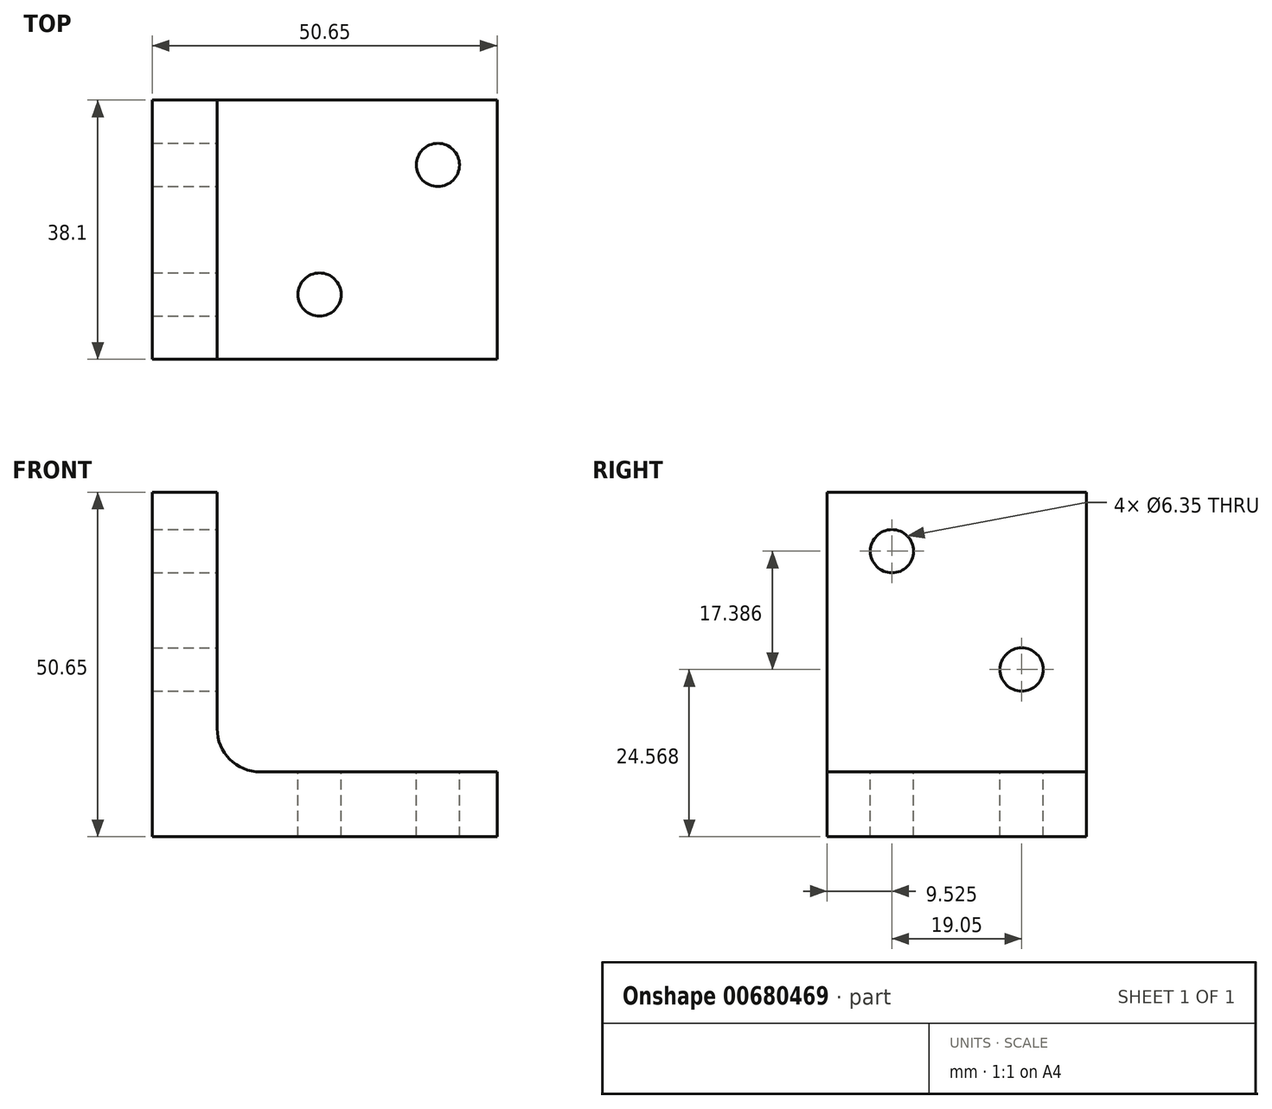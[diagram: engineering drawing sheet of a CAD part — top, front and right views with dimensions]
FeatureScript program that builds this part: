
annotation { "Feature Type Name" : "Feature", "Feature Type Description" : "" }
export const myFeature = defineFeature(function(context is Context, id is Id, definition is map)
    precondition{}
    {
        {
            var Q0;
            Q0=qCreatedBy(makeId("Front.planeOp"),FACE);
            var sketch = newSketch(context, id + "F0", { "sketchPlane" : qUnion([Q0])});
            skLineSegment(sketch, "E0.bottom", {"start": v(0, 0) * mm, "end": v(50.65, 0) * mm});
            skLineSegment(sketch, "E0.top", {"start": v(0, 50.65) * mm, "end": v(50.65, 50.65) * mm});
            skLineSegment(sketch, "E0.left", {"start": v(0, 0) * mm, "end": v(0, 50.65) * mm});
            skLineSegment(sketch, "E0.right", {"start": v(50.65, 0) * mm, "end": v(50.65, 50.65) * mm});
            skSolve(sketch);
        }
        {
            var Q0;
            Q0=makeQuery(id+"F0.imprint","IMPRINT",FACE,{"disambiguationData":[TD([[makeQuery(id+"F0.imprint","IMPRINT",EDGE,{"derivedFrom":sQuery(id+"F0.wireOp",EDGE,"E0.bottom")}),1.0]])]});
            extrude(context, id + "F1", {"entities" : qUnion([Q0]), "depth" : 38.1 * mm, "offsetDistance" : 25.4 * mm});
        }
        {
            var Q0;
            Q0=makeQuery(id+"F1.opExtrude","CAP_FACE",FACE,{"disambiguationData":[OSD([sQuery(id+"F0.wireOp",EDGE,"E0.bottom"),sQuery(id+"F0.wireOp",EDGE,"E0.top"),sQuery(id+"F0.wireOp",EDGE,"E0.left"),sQuery(id+"F0.wireOp",EDGE,"E0.right")])],"isStart":false});
            var sketch = newSketch(context, id + "F2", { "sketchPlane" : qUnion([Q0])});
            skLineSegment(sketch, "E1.bottom", {"start": v(50.65, 50.65) * mm, "end": v(9.52, 50.65) * mm});
            skLineSegment(sketch, "E1.top", {"start": v(50.65, 9.52) * mm, "end": v(15.88, 9.52) * mm});
            skLineSegment(sketch, "E1.left", {"start": v(50.65, 50.65) * mm, "end": v(50.65, 9.52) * mm});
            skLineSegment(sketch, "E1.right", {"start": v(9.52, 50.65) * mm, "end": v(9.53, 15.87) * mm});
            skPoint(sketch, "E2.visualSharp", {"position": v(9.53, 9.52) * mm});
            skArc(sketch, "E2.filletArc", {"start": v(9.53, 15.87) * mm, "mid": v(11.38, 11.38) * mm, "end": v(15.88, 9.52) * mm});
            skSolve(sketch);
        }
        {
            var Q0;
            Q0=makeQuery(id+"F2.imprint","IMPRINT",FACE,{"disambiguationData":[TD([[makeQuery(id+"F2.imprint","IMPRINT",EDGE,{"derivedFrom":sQuery(id+"F2.wireOp",EDGE,"E1.bottom")}),-1.0]])]});
            extrude(context, id + "F3", {"entities" : qUnion([Q0]), "operationType" : NewBodyOperationType.REMOVE, "endBound" : BoundingType.THROUGH_ALL, "oppositeDirection" : true, "depth" : 25.4 * mm, "offsetDistance" : 25.4 * mm});
        }
        {
            var Q0;
            Q0=makeQuery(id+"F3.boolean.opBoolean","COPY",FACE,{"derivedFrom":makeQuery(id+"F3.opExtrude","SWEPT_FACE",FACE,{"disambiguationData":[OSD([sQuery(id+"F2.wireOp",EDGE,"E1.top")])]})});
            var sketch = newSketch(context, id + "F4", { "sketchPlane" : qUnion([Q0])});
            skCircle(sketch, "E3", {"center": v(41.95, -9.53) * mm, "radius": 3.18 * mm});
            skLineSegment(sketch, "E4", {"start": v(15.88, -19.05) * mm, "end": v(50.65, -19.05) * mm, "construction": true});
            skLineSegment(sketch, "E5", {"start": v(33.26, 0) * mm, "end": v(33.26, -38.1) * mm, "construction": true});
            skLineSegment(sketch, "E6", {"start": v(33.26, -19.05) * mm, "end": v(50.65, 0) * mm, "construction": true});
            skLineSegment(sketch, "E7", {"start": v(33.26, -19.05) * mm, "end": v(15.88, -38.1) * mm, "construction": true});
            skCircle(sketch, "E8", {"center": v(24.57, -28.58) * mm, "radius": 3.18 * mm});
            skSolve(sketch);
        }
        {
            var Q0;
            Q0=makeQuery(id+"F4.imprint","IMPRINT",FACE,{"disambiguationData":[TD([[makeQuery(id+"F4.imprint","IMPRINT",EDGE,{"derivedFrom":sQuery(id+"F4.wireOp",EDGE,"E8")}),1.0]])]});
            var Q1;
            Q1=makeQuery(id+"F4.imprint","IMPRINT",FACE,{"disambiguationData":[TD([[makeQuery(id+"F4.imprint","IMPRINT",EDGE,{"derivedFrom":sQuery(id+"F4.wireOp",EDGE,"E3")}),1.0]])]});
            extrude(context, id + "F5", {"entities" : qUnion([Q0, Q1]), "operationType" : NewBodyOperationType.REMOVE, "endBound" : BoundingType.THROUGH_ALL, "oppositeDirection" : true, "depth" : 25.4 * mm, "offsetDistance" : 25.4 * mm});
        }
        {
            var Q0;
            Q0=makeQuery(id+"F3.boolean.opBoolean","COPY",FACE,{"derivedFrom":makeQuery(id+"F3.opExtrude","SWEPT_FACE",FACE,{"disambiguationData":[OSD([sQuery(id+"F2.wireOp",EDGE,"E1.right")])]})});
            var sketch = newSketch(context, id + "F6", { "sketchPlane" : qUnion([Q0])});
            skLineSegment(sketch, "E9", {"start": v(-38.1, 33.26) * mm, "end": v(0, 33.26) * mm, "construction": true});
            skLineSegment(sketch, "E10", {"start": v(-19.05, 50.65) * mm, "end": v(-19.05, 15.87) * mm, "construction": true});
            skLineSegment(sketch, "E11", {"start": v(-19.05, 33.26) * mm, "end": v(-38.1, 50.65) * mm, "construction": true});
            skLineSegment(sketch, "E12", {"start": v(0, 15.87) * mm, "end": v(-19.05, 33.26) * mm, "construction": true});
            skCircle(sketch, "E13", {"center": v(-28.57, 41.95) * mm, "radius": 3.18 * mm});
            skCircle(sketch, "E14", {"center": v(-9.53, 24.57) * mm, "radius": 3.18 * mm});
            skSolve(sketch);
        }
        {
            var Q0;
            Q0=makeQuery(id+"F6.imprint","IMPRINT",FACE,{"disambiguationData":[TD([[makeQuery(id+"F6.imprint","IMPRINT",EDGE,{"derivedFrom":sQuery(id+"F6.wireOp",EDGE,"E13")}),1.0]])]});
            var Q1;
            Q1=makeQuery(id+"F6.imprint","IMPRINT",FACE,{"disambiguationData":[TD([[makeQuery(id+"F6.imprint","IMPRINT",EDGE,{"derivedFrom":sQuery(id+"F6.wireOp",EDGE,"E14")}),1.0]])]});
            extrude(context, id + "F7", {"entities" : qUnion([Q0, Q1]), "operationType" : NewBodyOperationType.REMOVE, "endBound" : BoundingType.THROUGH_ALL, "oppositeDirection" : true, "depth" : 25.4 * mm, "offsetDistance" : 25.4 * mm});
        }
    });
